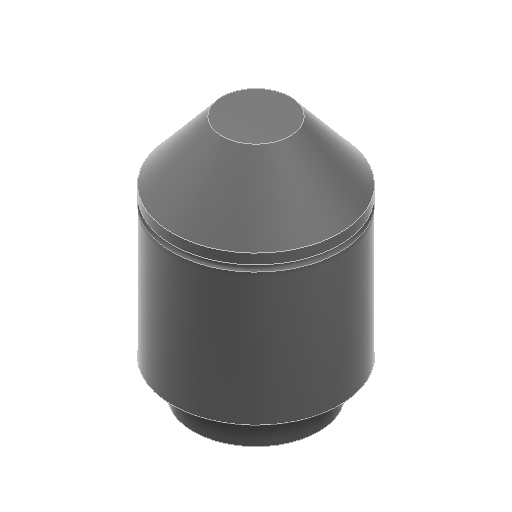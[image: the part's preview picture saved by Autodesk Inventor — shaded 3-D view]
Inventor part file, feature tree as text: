
AUTODESK INVENTOR PART (.ipt)
format: ipt  version: 2024.1 (Build 281209000, 209)  size: 154,112 bytes
history: native  units: mm
features: revolve x1, sketch x1
ambient origin geometry x8: Origin, YZ Plane, XZ Plane, XY Plane, X Axis, Y Axis, Z Axis, Center Point
bodies: Volumenkörper1 (feature_tree)
feature tree (2):
  revolve  "Umdrehung1"
  sketch  "Skizze1"  dims[d0=24.0mm d1=24.43461mm d2=5.5mm d3=1.0mm d4=0.5mm d5=1.65mm d6=0.5mm d7=12.225mm d8=4.93mm d9=10.08mm d10=90.0deg]
